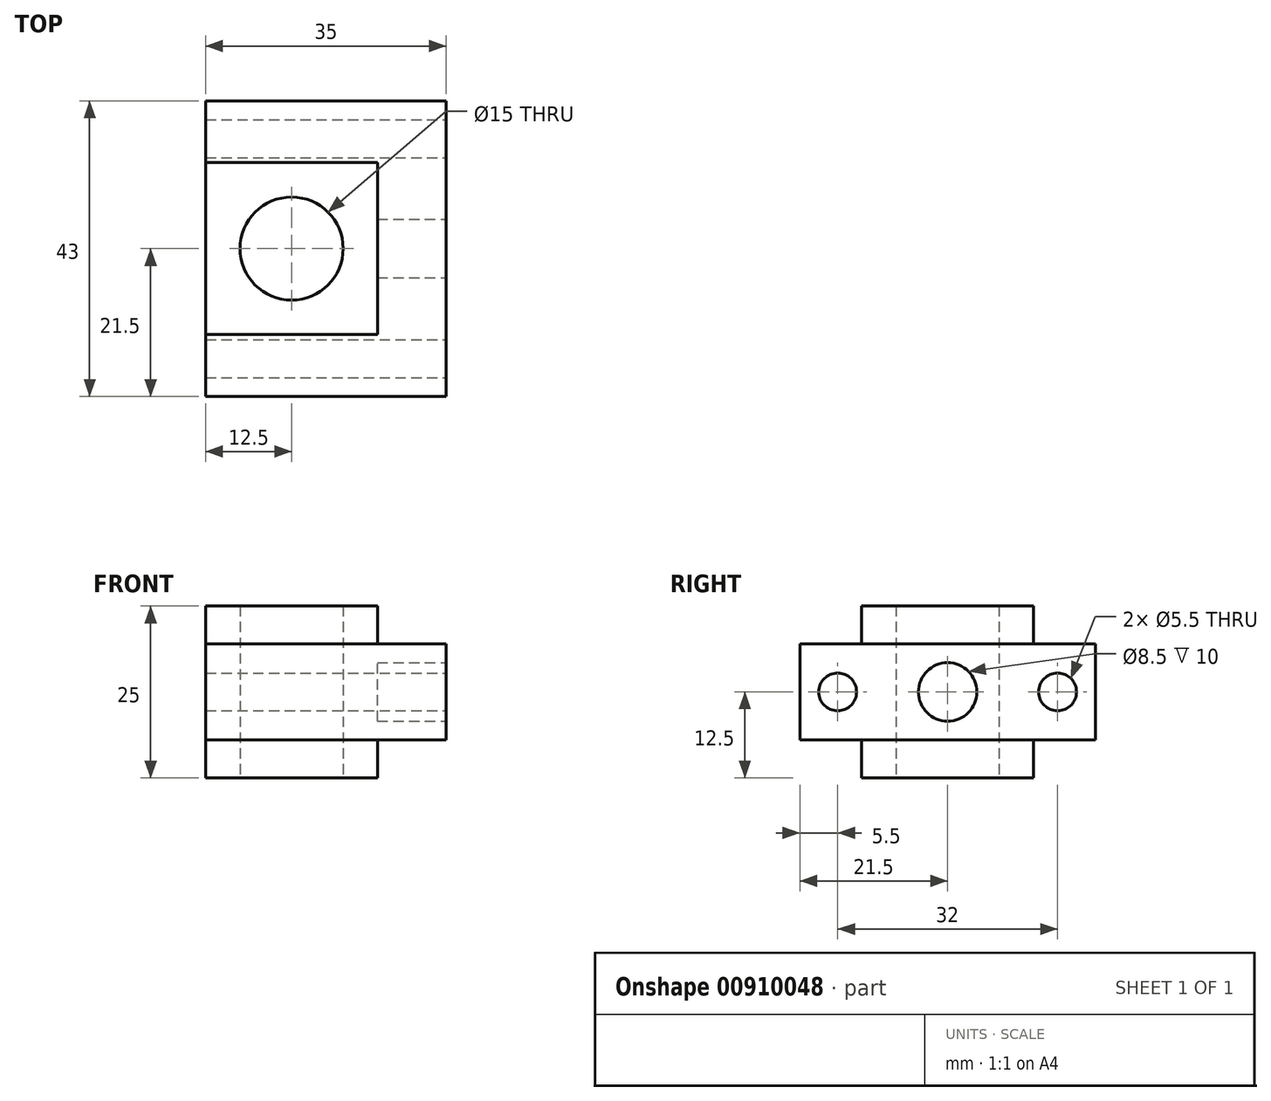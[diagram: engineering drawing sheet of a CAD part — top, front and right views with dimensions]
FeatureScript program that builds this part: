
annotation { "Feature Type Name" : "Feature", "Feature Type Description" : "" }
export const myFeature = defineFeature(function(context is Context, id is Id, definition is map)
    precondition{}
    {
        {
            var Q0;
            Q0=qCreatedBy(makeId("Top.planeOp"),FACE);
            var sketch = newSketch(context, id + "F0", { "sketchPlane" : qUnion([Q0])});
            skLineSegment(sketch, "E0.bottom", {"start": v(0, 0) * mm, "end": v(25, 0) * mm});
            skLineSegment(sketch, "E0.top", {"start": v(0, 25) * mm, "end": v(25, 25) * mm});
            skLineSegment(sketch, "E0.left", {"start": v(0, 0) * mm, "end": v(0, 25) * mm});
            skLineSegment(sketch, "E0.right", {"start": v(25, 0) * mm, "end": v(25, 25) * mm});
            skCircle(sketch, "E1", {"center": v(12.5, 12.5) * mm, "radius": 7.5 * mm});
            skPoint(sketch, "E1.centerSnap0", {"position": v(0, 12.5) * mm});
            skPoint(sketch, "E1.centerSnap1", {"position": v(12.5, 0) * mm});
            skSolve(sketch);
        }
        {
            var Q0;
            Q0=makeQuery(id+"F0.imprint","IMPRINT",FACE,{"disambiguationData":[TD([[makeQuery(id+"F0.imprint","IMPRINT",EDGE,{"derivedFrom":sQuery(id+"F0.wireOp",EDGE,"E0.bottom")}),1.0]])]});
            extrude(context, id + "F1", {"entities" : qUnion([Q0]), "depth" : 12.5 * mm, "offsetDistance" : 25 * mm, "hasSecondDirection" : true, "secondDirectionOppositeDirection" : true, "secondDirectionDepth" : 12.5 * mm});
        }
        {
            var Q0;
            Q0=qCreatedBy(makeId("Top.planeOp"),FACE);
            var sketch = newSketch(context, id + "F2", { "sketchPlane" : qUnion([Q0])});
            skLineSegment(sketch, "E2", {"start": v(0, 25) * mm, "end": v(12.5, 25) * mm});
            skLineSegment(sketch, "E3", {"start": v(0, 0) * mm, "end": v(0, 25) * mm});
            skLineSegment(sketch, "E4", {"start": v(0, 0) * mm, "end": v(12.5, 0) * mm});
            skLineSegment(sketch, "E5", {"start": v(12.5, 12.5) * mm, "end": v(12.5, -9) * mm});
            skPoint(sketch, "E5.startSnap0", {"position": v(0, 12.5) * mm});
            skLineSegment(sketch, "E6", {"start": v(12.5, 12.5) * mm, "end": v(12.5, 34) * mm});
            skLineSegment(sketch, "E7", {"start": v(12.5, 34) * mm, "end": v(35, 34) * mm});
            skLineSegment(sketch, "E8", {"start": v(35, 34) * mm, "end": v(35, -9) * mm});
            skLineSegment(sketch, "E9", {"start": v(35, -9) * mm, "end": v(12.5, -9) * mm});
            skCircle(sketch, "E10", {"center": v(12.5, 12.5) * mm, "radius": 7.5 * mm});
            skLineSegment(sketch, "E11", {"start": v(12.5, -9) * mm, "end": v(0, -9) * mm});
            skLineSegment(sketch, "E12", {"start": v(0, -9) * mm, "end": v(0, 0) * mm});
            skLineSegment(sketch, "E13", {"start": v(0, 25) * mm, "end": v(0, 34) * mm});
            skLineSegment(sketch, "E14", {"start": v(0, 34) * mm, "end": v(12.5, 34) * mm});
            skSolve(sketch);
        }
        {
            var Q0;
            {var subQ2=sQuery(id+"F2.wireOp",EDGE,"E7");Q0=makeQuery(id+"F2.imprint","IMPRINT",FACE,{"disambiguationData":[TD([[makeQuery(id+"F2.imprint","IMPRINT",EDGE,{"derivedFrom":subQ2}),-1.0]])]});}
            var Q1;
            {var subQ0=sQuery(id+"F2.wireOp",EDGE,"E2");Q1=makeQuery(id+"F2.imprint","IMPRINT",FACE,{"disambiguationData":[TD([[makeQuery(id+"F2.imprint","IMPRINT",EDGE,{"derivedFrom":subQ0}),1.0]])]});}
            var Q2;
            {var subQ0=sQuery(id+"F2.wireOp",EDGE,"E4");Q2=makeQuery(id+"F2.imprint","IMPRINT",FACE,{"disambiguationData":[TD([[makeQuery(id+"F2.imprint","IMPRINT",EDGE,{"derivedFrom":subQ0}),-1.0]])]});}
            extrude(context, id + "F3", {"entities" : qUnion([Q0, Q1, Q2]), "operationType" : NewBodyOperationType.ADD, "depth" : 7 * mm, "offsetDistance" : 25 * mm, "hasSecondDirection" : true, "secondDirectionOppositeDirection" : true, "secondDirectionDepth" : 7 * mm});
        }
        {
            var Q0;
            Q0=makeQuery(id+"F3.opExtrude","SWEPT_FACE",FACE,{"disambiguationData":[OSD([sQuery(id+"F2.wireOp",EDGE,"E8")])]});
            var sketch = newSketch(context, id + "F4", { "sketchPlane" : qUnion([Q0])});
            skLineSegment(sketch, "E15", {"start": v(0, 0) * mm, "end": v(12.5, 0) * mm});
            skCircle(sketch, "E16", {"center": v(12.5, 0) * mm, "radius": 4.25 * mm});
            skSolve(sketch);
        }
        {
            var Q0;
            Q0=makeQuery(id+"F4.imprint","IMPRINT",FACE,{"disambiguationData":[TD([[makeQuery(id+"F4.imprint","IMPRINT",EDGE,{"derivedFrom":sQuery(id+"F4.wireOp",EDGE,"E16")}),-1.0]])]});
            var sketch = newSketch(context, id + "F5", { "sketchPlane" : qUnion([Q0])});
            skLineSegment(sketch, "E17", {"start": v(0, 0) * mm, "end": v(12.5, 0) * mm});
            skLineSegment(sketch, "E18", {"start": v(12.5, 0) * mm, "end": v(-3.5, 0) * mm});
            skLineSegment(sketch, "E19", {"start": v(12.5, 0) * mm, "end": v(28.5, 0) * mm});
            skCircle(sketch, "E20", {"center": v(-3.5, 0) * mm, "radius": 2.75 * mm});
            skCircle(sketch, "E21", {"center": v(28.5, 0) * mm, "radius": 2.75 * mm});
            skSolve(sketch);
        }
        {
            var Q0;
            Q0=makeQuery(id+"F4.imprint","IMPRINT",FACE,{"disambiguationData":[TD([[makeQuery(id+"F4.imprint","IMPRINT",EDGE,{"derivedFrom":sQuery(id+"F4.wireOp",EDGE,"E16")}),1.0]])]});
            extrude(context, id + "F6", {"entities" : qUnion([Q0]), "operationType" : NewBodyOperationType.REMOVE, "oppositeDirection" : true, "depth" : 10 * mm, "offsetDistance" : 25 * mm});
        }
        {
            var Q0;
            Q0=makeQuery(id+"F5.imprint","IMPRINT",FACE,{"disambiguationData":[TD([[makeQuery(id+"F5.imprint","IMPRINT",EDGE,{"derivedFrom":sQuery(id+"F5.wireOp",EDGE,"E21")}),1.0]])]});
            var Q1;
            Q1=makeQuery(id+"F5.imprint","IMPRINT",FACE,{"disambiguationData":[TD([[makeQuery(id+"F5.imprint","IMPRINT",EDGE,{"derivedFrom":sQuery(id+"F5.wireOp",EDGE,"E20")}),1.0]])]});
            extrude(context, id + "F7", {"entities" : qUnion([Q0, Q1]), "operationType" : NewBodyOperationType.REMOVE, "oppositeDirection" : true, "depth" : 35.1 * mm, "offsetDistance" : 25 * mm});
        }
    });
